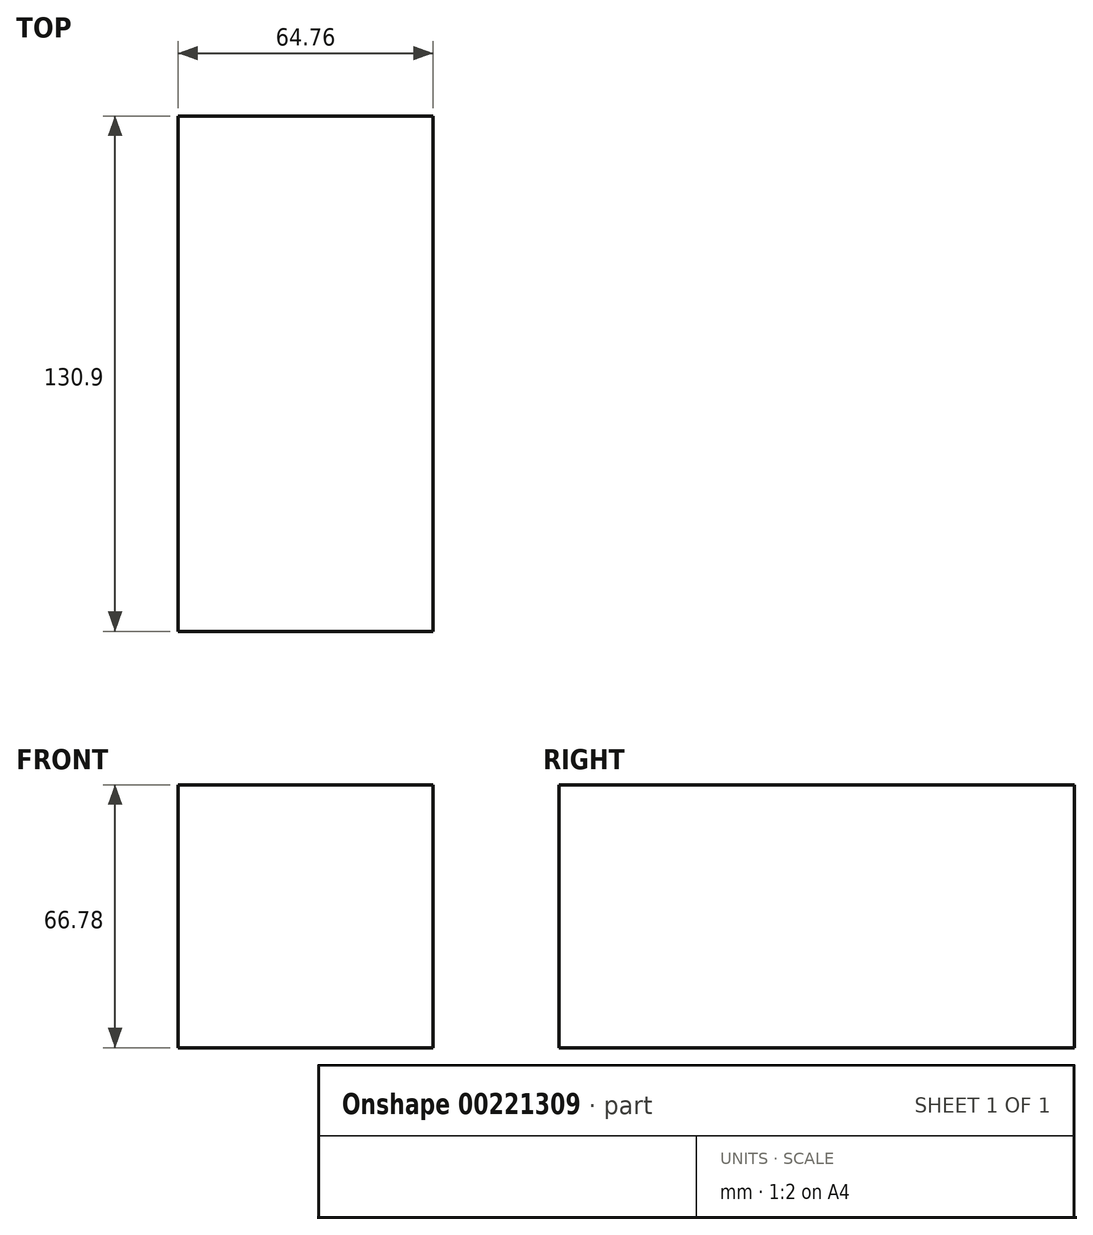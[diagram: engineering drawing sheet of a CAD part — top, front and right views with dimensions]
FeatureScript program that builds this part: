
annotation { "Feature Type Name" : "Feature", "Feature Type Description" : "" }
export const myFeature = defineFeature(function(context is Context, id is Id, definition is map)
    precondition{}
    {
        {
            var Q0;
            Q0=qCreatedBy(makeId("Front.planeOp"),FACE);
            var sketch = newSketch(context, id + "F0", { "sketchPlane" : qUnion([Q0])});
            skLineSegment(sketch, "E0.bottom", {"start": v(-134.45, 52.74) * mm, "end": v(-69.69, 52.74) * mm});
            skLineSegment(sketch, "E0.top", {"start": v(-134.45, -14.04) * mm, "end": v(-69.69, -14.04) * mm});
            skLineSegment(sketch, "E0.left", {"start": v(-134.45, 52.74) * mm, "end": v(-134.45, -14.04) * mm});
            skLineSegment(sketch, "E0.right", {"start": v(-69.69, 52.74) * mm, "end": v(-69.69, -14.04) * mm});
            skSolve(sketch);
        }
        {
            var Q0;
            Q0=makeQuery(id+"F0.imprint","IMPRINT",FACE,{"disambiguationData":[TD([[makeQuery(id+"F0.imprint","IMPRINT",EDGE,{"derivedFrom":sQuery(id+"F0.wireOp",EDGE,"E0.bottom")}),-1.0]])]});
            extrude(context, id + "F1", {"entities" : qUnion([Q0]), "depth" : 130.9 * mm});
        }
    });
